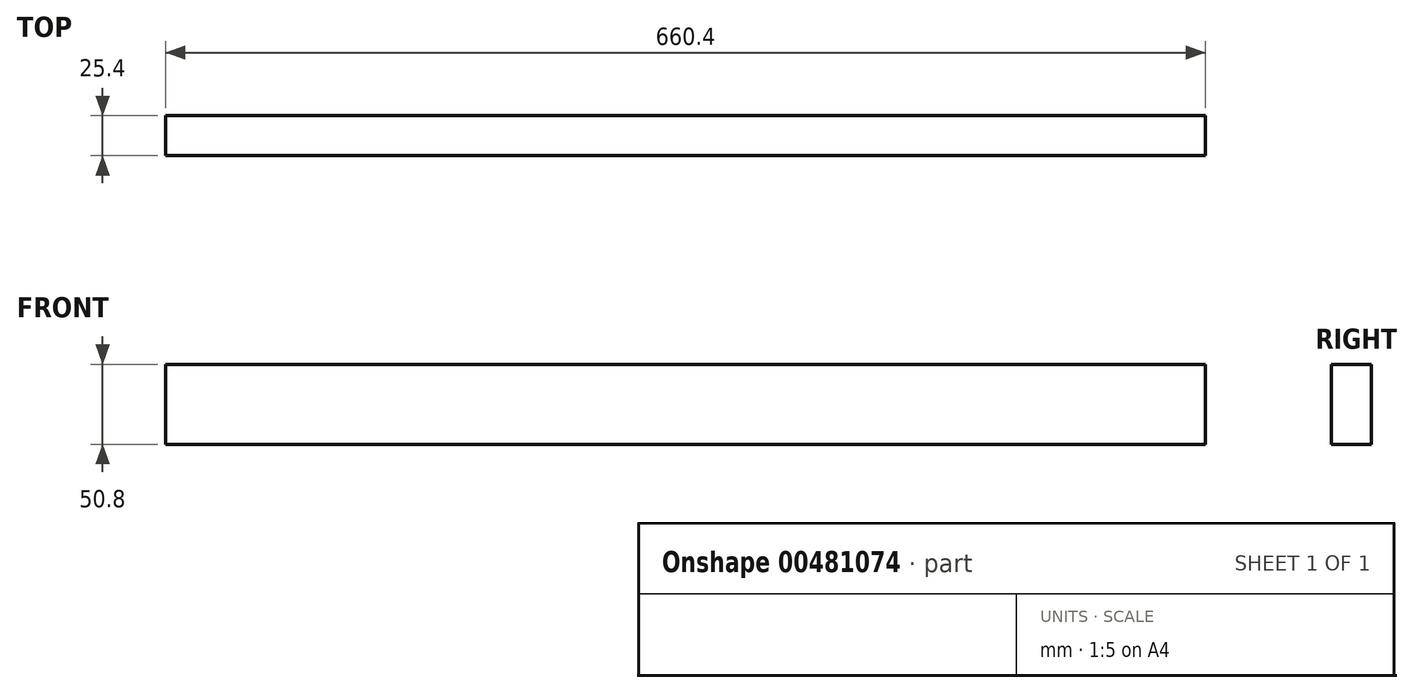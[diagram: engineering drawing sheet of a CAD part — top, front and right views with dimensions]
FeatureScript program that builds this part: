
annotation { "Feature Type Name" : "Feature", "Feature Type Description" : "" }
export const myFeature = defineFeature(function(context is Context, id is Id, definition is map)
    precondition{}
    {
        {
            var Q0;
            Q0=qCreatedBy(makeId("Top.planeOp"),FACE);
            var sketch = newSketch(context, id + "F0", { "sketchPlane" : qUnion([Q0])});
            skLineSegment(sketch, "E0.bottom", {"start": v(0, 0) * mm, "end": v(-660.4, 0) * mm});
            skLineSegment(sketch, "E0.top", {"start": v(0, 25.4) * mm, "end": v(-660.4, 25.4) * mm});
            skLineSegment(sketch, "E0.left", {"start": v(0, 0) * mm, "end": v(0, 25.4) * mm});
            skLineSegment(sketch, "E0.right", {"start": v(-660.4, 0) * mm, "end": v(-660.4, 25.4) * mm});
            skSolve(sketch);
        }
        {
            var Q0;
            Q0=makeQuery(id+"F0.imprint","IMPRINT",FACE,{"disambiguationData":[TD([[makeQuery(id+"F0.imprint","IMPRINT",EDGE,{"derivedFrom":sQuery(id+"F0.wireOp",EDGE,"E0.bottom")}),-1.0]])]});
            extrude(context, id + "F1", {"entities" : qUnion([Q0]), "depth" : 50.8 * mm});
        }
    });
